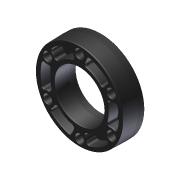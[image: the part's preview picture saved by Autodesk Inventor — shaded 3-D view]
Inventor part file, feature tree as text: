
AUTODESK INVENTOR PART (.ipt)
format: ipt  version: 2011 (Build 150239000, 239)  size: 592,384 bytes
history: native  units: in
note: dims shown in document units (in); Inventor stores cm internally (conversion verified against a paired STEP export)
features: fillet x2, imported_body x2
ambient origin geometry x8: Origin, YZ Plane, XZ Plane, XY Plane, X Axis, Y Axis, Z Axis, Center Point
feature tree (4):
  fillet  "Fillet2"  [1 undecoded]
  imported_body  "Base1"
  imported_body  "Base2"
  fillet  "Fillet1"  [1 undecoded]
note: 2 required parameter values undecoded (feature->parameter linkage not recoverable at this tier; creation-order binding heuristic only, values carry confidence <= 0.55)
